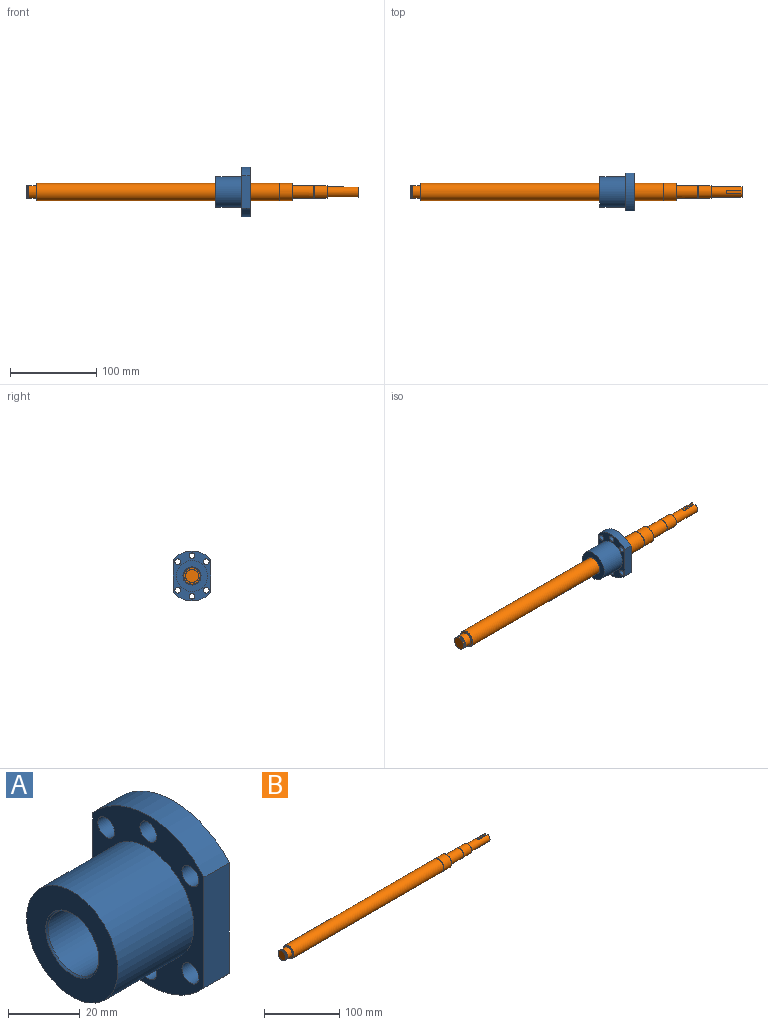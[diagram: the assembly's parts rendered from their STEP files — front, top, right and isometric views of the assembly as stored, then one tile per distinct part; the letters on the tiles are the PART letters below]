
ASSEMBLY  parts=2 mates=1
PART A: 17 faces, bbox 40x44x58 mm
  f0: cylinder r=18mm len=36mm, axis (1,0,0), area 3392.9mm2, adj f1,f7
  f1: plane 36x36mm, normal (-1,0,0), area 671.5mm2, adj f0,f9
  f2: plane 37.79x10mm, normal (0,1,0), area 377.9mm2, adj f3,f5,f6,f7
  f3: cylinder r=29mm len=44mm, axis (-1,0,0), area 499.5mm2, adj f2,f4,f6,f7
  f4: plane 37.79x10mm, normal (0,-1,0), area 377.9mm2, adj f3,f5,f6,f7
  f5: cylinder r=29mm len=44mm, axis (-1,0,0), area 499.5mm2, adj f2,f4,f6,f7
  f6: plane 58x44mm, normal (1,0,0), area 1728.3mm2, adj f2,f3,f4,f5,f10,f11,f12,f13
  f7: plane 58x44mm, normal (-1,0,0), area 1056.7mm2, adj f0,f2,f3,f4,f5,f11,f12,f13
  f8: cylinder r=10mm len=39mm, axis (1,0,0), area 2450.4mm2, adj f9,f10
  f9: cone r=10.5mm half-angle=45deg, axis (-1,0,0), area 45.5mm2, adj f1,f8
  f10: cone r=10mm half-angle=45deg, axis (1,0,0), area 45.5mm2, adj f6,f8
  f11: cylinder r=3.3mm len=10mm, axis (1,0,0), area 207.3mm2, adj f6,f7
  f12: cylinder r=3.3mm len=10mm, axis (1,0,0), area 207.3mm2, adj f6,f7
  f13: cylinder r=3.3mm len=10mm, axis (1,0,0), area 207.3mm2, adj f6,f7
  f14: cylinder r=3.3mm len=10mm, axis (1,0,0), area 207.3mm2, adj f6,f7
  f15: cylinder r=3.3mm len=10mm, axis (1,0,0), area 207.3mm2, adj f6,f7
  f16: cylinder r=3.3mm len=10mm, axis (1,0,0), area 207.3mm2, adj f6,f7
PART B: 24 faces, bbox 386x20x20 mm
  f0: cylinder r=6mm len=36mm, axis (-1,0,0), area 1285.5mm2, adj f1,f18,f20,f21,f23
  f1: plane 12x11.66mm, normal (1,0,0), area 103.5mm2, adj f0,f20,f21,f22
  f2: cylinder r=7.5mm len=15mm, axis (1,0,0), area 424.1mm2, adj f3,f9
  f3: plane 15x15mm, normal (-1,0,0), area 16.1mm2, adj f2,f4
  f4: cylinder r=7.15mm len=14.3mm, axis (1,0,0), area 51.7mm2, adj f3,f7
  f5: cylinder r=7.5mm len=15mm, axis (1,0,0), area 87.2mm2, adj f6,f7
  f6: plane 15x15mm, normal (-1,0,0), area 176.7mm2, adj f5
  f7: plane 15x15mm, normal (1,0,0), area 16.1mm2, adj f4,f5
  f8: cylinder r=10mm len=282mm, axis (-1,0,0), area 17718.6mm2, adj f10,f11
  f9: plane 19x19mm, normal (-1,0,0), area 106.8mm2, adj f2,f10
  f10: cone r=10mm half-angle=45deg, axis (1,0,0), area 43.3mm2, adj f8,f9
  f11: cone r=9.5mm half-angle=45deg, axis (-1,0,0), area 43.3mm2, adj f8,f14
  f12: cylinder r=10mm len=20mm, axis (-1,0,0), area 942.5mm2, adj f13,f14
  f13: plane 20x20mm, normal (1,0,0), area 137.4mm2, adj f12,f15
  f14: plane 20x20mm, normal (-1,0,0), area 30.6mm2, adj f11,f12
  f15: cylinder r=7.5mm len=24.5mm, axis (-1,0,0), area 1154.5mm2, adj f13,f16
  f16: cone r=7mm half-angle=45deg, axis (-1,0,0), area 32.2mm2, adj f15,f19
  f17: cylinder r=7.5mm len=15mm, axis (-1,0,0), area 706.9mm2, adj f18,f19
  f18: plane 15x15mm, normal (1,0,0), area 63.6mm2, adj f0,f17
  f19: plane 15x15mm, normal (-1,0,0), area 22.8mm2, adj f16,f17
  f20: plane 16x2.16mm, normal (0,1,0), area 34.5mm2, adj f0,f1,f22,f23
  f21: plane 16x2.16mm, normal (0,-1,0), area 34.5mm2, adj f0,f1,f22,f23
  f22: plane 18x4mm, normal (0,0,1), area 70.3mm2, adj f1,f20,f21,f23
  f23: cylinder r=2mm len=4mm, axis (0,0,1), area 14.6mm2, adj f0,f20,f21,f22
PLACE A t=(-57.21,-23,-20.9)mm
PLACE B t=(-295.91,-23,-20.9)mm
MATE cylindrical A.f0 <-> B.f0  axis (1,0,0) through (-47.21,-23,-20.9)mm
